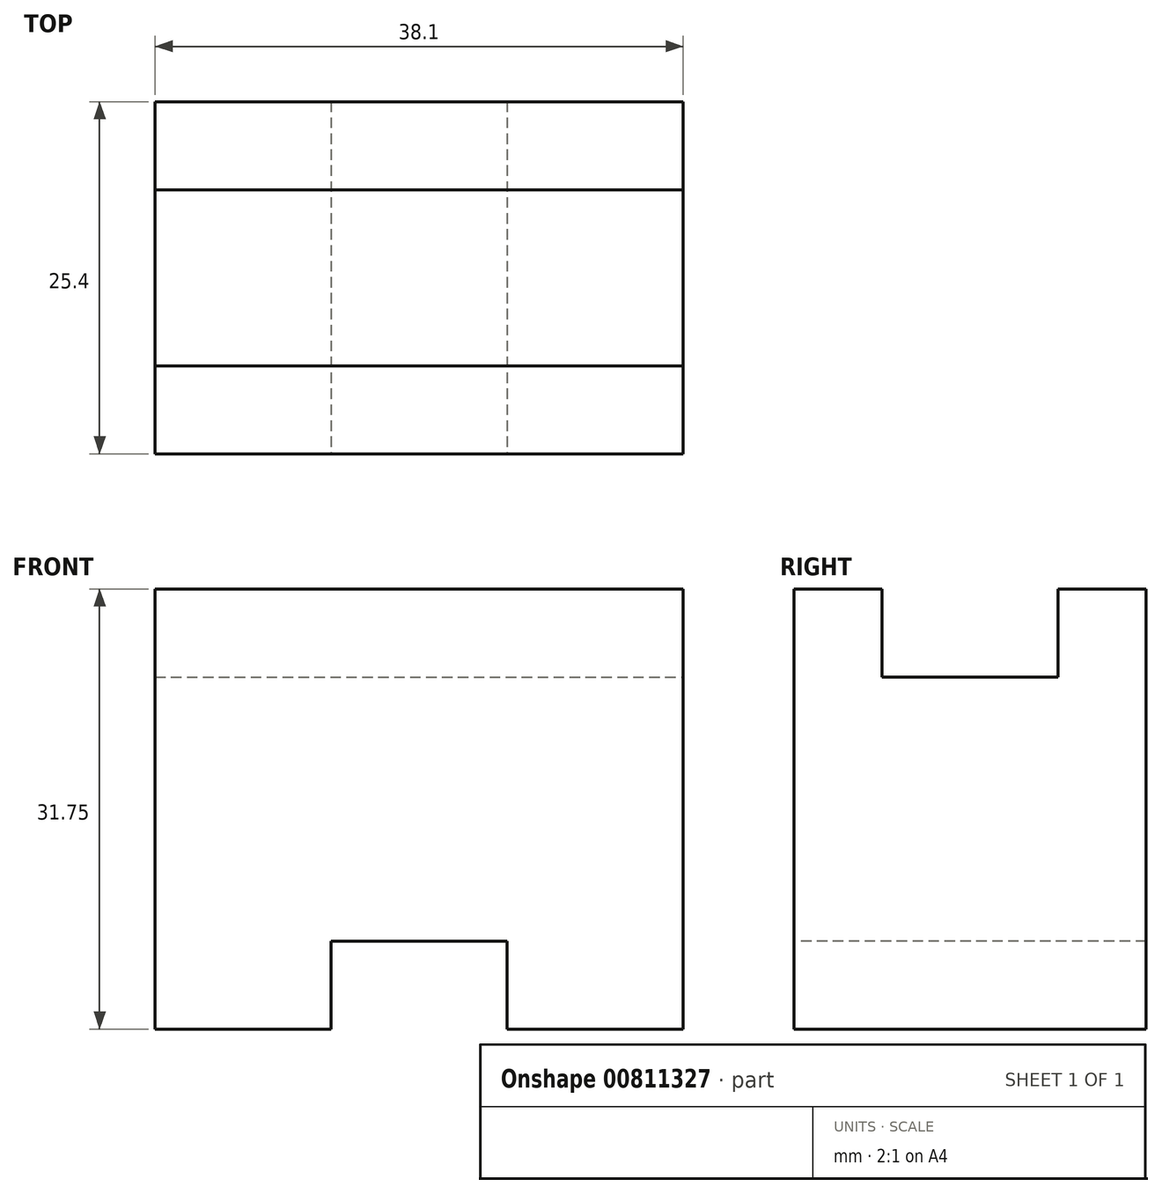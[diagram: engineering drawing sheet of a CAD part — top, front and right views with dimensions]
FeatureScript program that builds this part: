
annotation { "Feature Type Name" : "Feature", "Feature Type Description" : "" }
export const myFeature = defineFeature(function(context is Context, id is Id, definition is map)
    precondition{}
    {
        {
            var Q0;
            Q0=qCreatedBy(makeId("Right.planeOp"),FACE);
            var sketch = newSketch(context, id + "F0", { "sketchPlane" : qUnion([Q0])});
            skLineSegment(sketch, "E0", {"start": v(0, 0) * mm, "end": v(0, 31.75) * mm});
            skLineSegment(sketch, "E1", {"start": v(0, 31.75) * mm, "end": v(25.4, 31.75) * mm});
            skLineSegment(sketch, "E2", {"start": v(25.4, 31.75) * mm, "end": v(25.4, 0) * mm});
            skLineSegment(sketch, "E3", {"start": v(0, 0) * mm, "end": v(25.4, 0) * mm});
            skSolve(sketch);
        }
        {
            var Q0;
            Q0 = qSketchRegion(id + "F0", true);
            extrude(context, id + "F1", {"entities" : qUnion([Q0]), "depth" : 38.1 * mm, "offsetDistance" : 25.4 * mm});
        }
        {
            var Q0;
            Q0=makeQuery(id+"F1.opExtrude","CAP_FACE",FACE,{"disambiguationData":[OSD([sQuery(id+"F0.wireOp",EDGE,"E0"),sQuery(id+"F0.wireOp",EDGE,"E1"),sQuery(id+"F0.wireOp",EDGE,"E2"),sQuery(id+"F0.wireOp",EDGE,"E3")])],"isStart":false});
            var sketch = newSketch(context, id + "F2", { "sketchPlane" : qUnion([Q0])});
            skLineSegment(sketch, "E4", {"start": v(0, 31.75) * mm, "end": v(6.35, 31.75) * mm});
            skLineSegment(sketch, "E5", {"start": v(6.35, 31.75) * mm, "end": v(6.35, 25.4) * mm});
            skLineSegment(sketch, "E6", {"start": v(6.35, 25.4) * mm, "end": v(19.05, 25.4) * mm});
            skLineSegment(sketch, "E7", {"start": v(19.05, 25.4) * mm, "end": v(19.05, 31.75) * mm});
            skLineSegment(sketch, "E8", {"start": v(19.05, 31.75) * mm, "end": v(25.4, 31.75) * mm});
            skSolve(sketch);
        }
        {
            var Q0;
            Q0 = qSketchRegion(id + "F2", true);
            var Q1;
            {var subQ0=sQuery(id+"F2.wireOp",EDGE,"E5");Q1=makeQuery(id+"F2.imprint","IMPRINT",FACE,{"disambiguationData":[TD([[makeQuery(id+"F2.imprint","IMPRINT",EDGE,{"derivedFrom":subQ0}),1.0]])]});}
            extrude(context, id + "F3", {"entities" : qUnion([Q0, Q1]), "operationType" : NewBodyOperationType.REMOVE, "oppositeDirection" : true, "depth" : 38.1 * mm, "offsetDistance" : 25.4 * mm});
        }
        {
            var Q0;
            Q0=makeQuery(id+"F1.opExtrude","SWEPT_FACE",FACE,{"disambiguationData":[OSD([sQuery(id+"F0.wireOp",EDGE,"E0")])]});
            var sketch = newSketch(context, id + "F4", { "sketchPlane" : qUnion([Q0])});
            skLineSegment(sketch, "E9", {"start": v(0, 0) * mm, "end": v(12.7, 0) * mm});
            skLineSegment(sketch, "E10", {"start": v(12.7, 0) * mm, "end": v(12.7, 6.35) * mm});
            skLineSegment(sketch, "E11", {"start": v(12.7, 6.35) * mm, "end": v(25.4, 6.35) * mm});
            skLineSegment(sketch, "E12", {"start": v(25.4, 6.35) * mm, "end": v(25.4, 0) * mm});
            skLineSegment(sketch, "E13", {"start": v(25.4, 0) * mm, "end": v(38.1, 0) * mm});
            skSolve(sketch);
        }
        {
            var Q0;
            Q0 = qSketchRegion(id + "F4", true);
            var Q1;
            {var subQ0=sQuery(id+"F4.wireOp",EDGE,"E10");Q1=makeQuery(id+"F4.imprint","IMPRINT",FACE,{"disambiguationData":[TD([[makeQuery(id+"F4.imprint","IMPRINT",EDGE,{"derivedFrom":subQ0}),-1.0]])]});}
            extrude(context, id + "F5", {"entities" : qUnion([Q0, Q1]), "operationType" : NewBodyOperationType.REMOVE, "oppositeDirection" : true, "depth" : 31.75 * mm, "offsetDistance" : 25.4 * mm});
        }
    });
